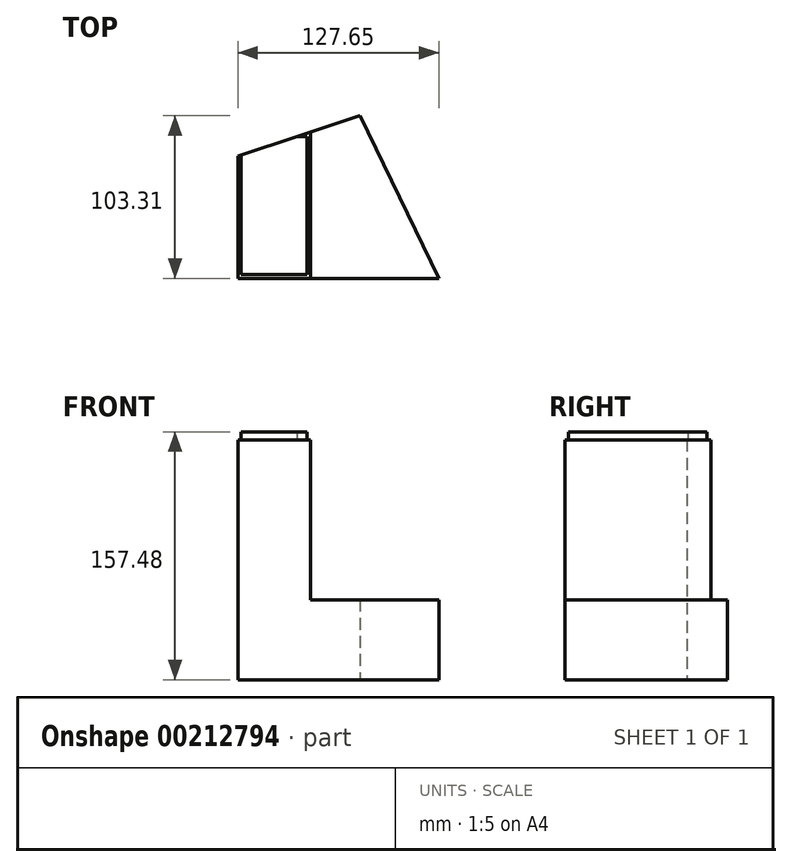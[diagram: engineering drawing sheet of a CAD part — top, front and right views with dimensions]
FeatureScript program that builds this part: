
annotation { "Feature Type Name" : "Feature", "Feature Type Description" : "" }
export const myFeature = defineFeature(function(context is Context, id is Id, definition is map)
    precondition{}
    {
        {
            var Q0;
            Q0=qCreatedBy(makeId("Top.planeOp"),FACE);
            var sketch = newSketch(context, id + "F0", { "sketchPlane" : qUnion([Q0])});
            skLineSegment(sketch, "E0.top", {"start": v(-38.84, -38.84) * mm, "end": v(38.84, -38.84) * mm});
            skLineSegment(sketch, "E0.left", {"start": v(-38.84, 38.84) * mm, "end": v(-38.84, -38.84) * mm});
            skPoint(sketch, "E0.middle", {"position": v(0, 0) * mm});
            skLineSegment(sketch, "E1", {"start": v(38.84, 64.47) * mm, "end": v(-38.84, 38.84) * mm});
            skLineSegment(sketch, "E2", {"start": v(38.84, -38.84) * mm, "end": v(88.81, -38.84) * mm});
            skLineSegment(sketch, "E3", {"start": v(88.81, -38.84) * mm, "end": v(38.84, 64.47) * mm});
            skPoint(sketch, "E4.start.orphan", {"position": v(38.84, 38.84) * mm});
            skLineSegment(sketch, "E5", {"start": v(7.12, 54) * mm, "end": v(7.12, -38.84) * mm});
            skSolve(sketch);
        }
        {
            var Q0;
            {var subQ0=sQuery(id+"F0.wireOp",EDGE,"E0.left");Q0=makeQuery(id+"F0.imprint","IMPRINT",FACE,{"disambiguationData":[TD([[makeQuery(id+"F0.imprint","IMPRINT",EDGE,{"derivedFrom":subQ0}),1.0]])]});}
            extrude(context, id + "F1", {"entities" : qUnion([Q0]), "depth" : 152.4 * mm});
        }
        {
            var Q0;
            {var subQ1=sQuery(id+"F0.wireOp",EDGE,"E2");Q0=makeQuery(id+"F0.imprint","IMPRINT",FACE,{"disambiguationData":[TD([[makeQuery(id+"F0.imprint","IMPRINT",EDGE,{"derivedFrom":subQ1}),1.0]])]});}
            extrude(context, id + "F2", {"entities" : qUnion([Q0]), "operationType" : NewBodyOperationType.ADD, "depth" : 50.8 * mm});
        }
        {
            var Q0;
            Q0=makeQuery(id+"F1.opExtrude","CAP_FACE",FACE,{"disambiguationData":[OSD([sQuery(id+"F0.wireOp",EDGE,"E0.top"),sQuery(id+"F0.wireOp",EDGE,"E0.left"),sQuery(id+"F0.wireOp",EDGE,"E1"),sQuery(id+"F0.wireOp",EDGE,"E5")])],"isStart":false});
            var sketch = newSketch(context, id + "F3", { "sketchPlane" : qUnion([Q0])});
            skLineSegment(sketch, "E6.bottom", {"start": v(5.01, 51.27) * mm, "end": v(-36.93, 51.27) * mm});
            skLineSegment(sketch, "E6.top", {"start": v(5.01, -36.5) * mm, "end": v(-36.93, -36.5) * mm});
            skLineSegment(sketch, "E6.left", {"start": v(5.01, 51.27) * mm, "end": v(5.01, -36.5) * mm});
            skLineSegment(sketch, "E6.right", {"start": v(-36.93, 51.27) * mm, "end": v(-36.93, -36.5) * mm});
            skSolve(sketch);
        }
        {
            var Q0;
            {var subQ1=sQuery(id+"F3.wireOp",EDGE,"E6.top");Q0=makeQuery(id+"F3.imprint","IMPRINT",FACE,{"disambiguationData":[TD([[makeQuery(id+"F3.imprint","IMPRINT",EDGE,{"derivedFrom":subQ1}),-1.0]])]});}
            extrude(context, id + "F4", {"entities" : qUnion([Q0]), "operationType" : NewBodyOperationType.ADD, "depth" : 5.08 * mm});
        }
    });
